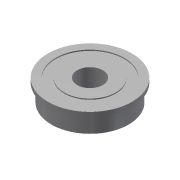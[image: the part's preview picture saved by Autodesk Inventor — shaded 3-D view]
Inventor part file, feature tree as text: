
AUTODESK INVENTOR PART (.ipt)
format: ipt  version: 2013 (Build 170138000, 138)  size: 114,688 bytes
history: native  units: in
note: dims shown in document units (in); Inventor stores cm internally (conversion verified against a paired STEP export)
features: revolve x1, imported_body x1
ambient origin geometry x8: Origin, YZ Plane, XZ Plane, XY Plane, X Axis, Y Axis, Z Axis, Center Point
feature tree (2):
  revolve  "Revolve1"  [1 undecoded]
  imported_body  "Base1"
note: 1 required parameter value undecoded (feature->parameter linkage not recoverable at this tier; creation-order binding heuristic only, values carry confidence <= 0.55)
